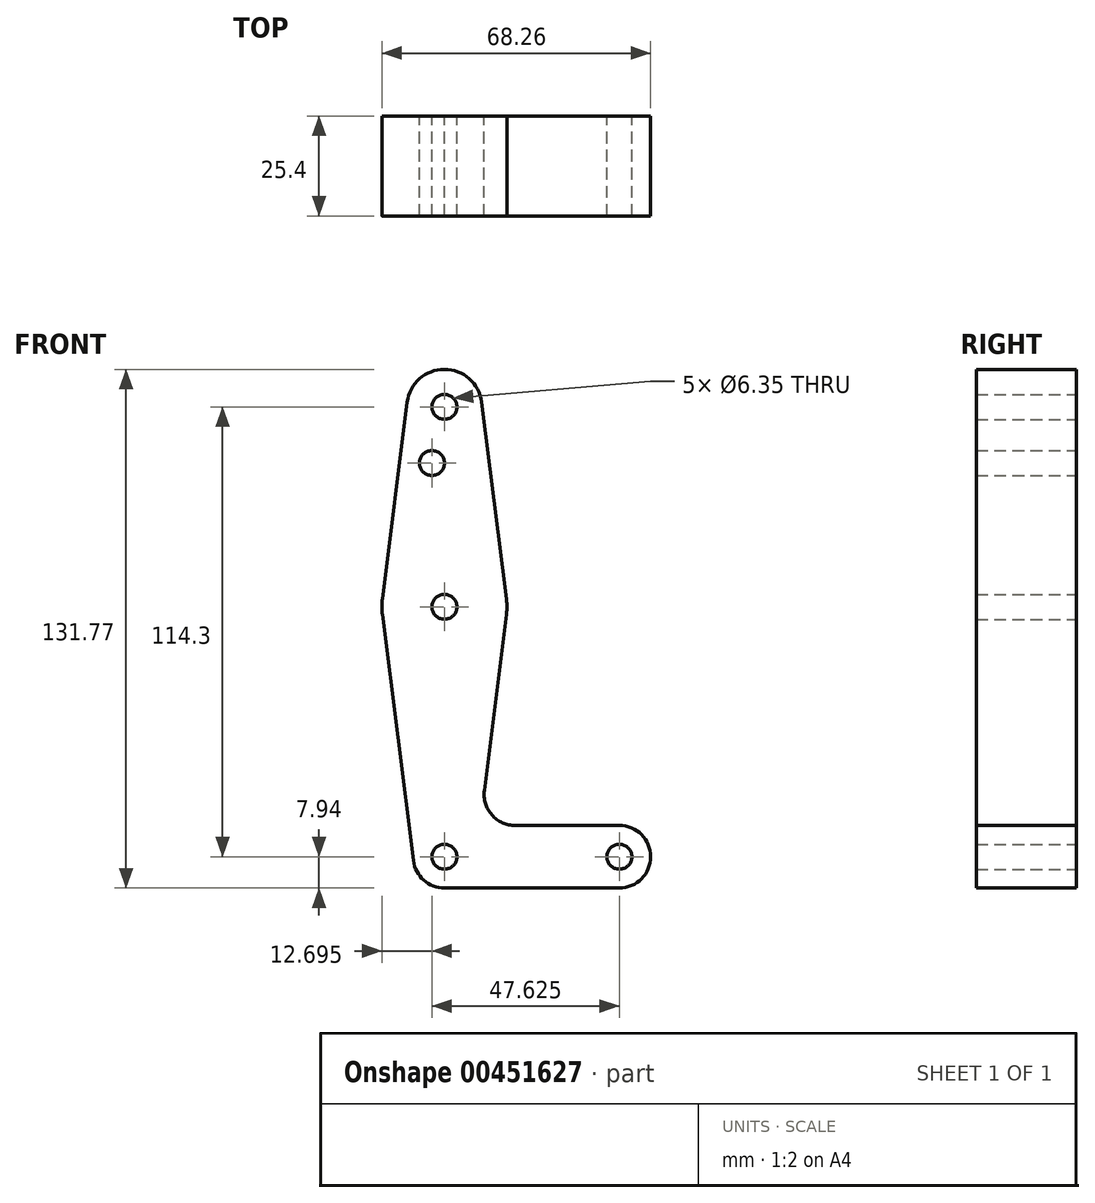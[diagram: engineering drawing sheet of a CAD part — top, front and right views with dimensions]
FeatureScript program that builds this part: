
annotation { "Feature Type Name" : "Feature", "Feature Type Description" : "" }
export const myFeature = defineFeature(function(context is Context, id is Id, definition is map)
    precondition{}
    {
        {
            var Q0;
            Q0=qCreatedBy(makeId("Front.planeOp"),FACE);
            var sketch = newSketch(context, id + "F0", { "sketchPlane" : qUnion([Q0])});
            skLineSegment(sketch, "E0", {"start": v(0, 0) * mm, "end": v(0, 114.3) * mm, "construction": true});
            skLineSegment(sketch, "E1", {"start": v(0, 0) * mm, "end": v(44.45, 0) * mm, "construction": true});
            skCircle(sketch, "E2", {"center": v(0, 114.3) * mm, "radius": 9.53 * mm});
            skCircle(sketch, "E3", {"center": v(0, 63.5) * mm, "radius": 15.88 * mm});
            skCircle(sketch, "E4", {"center": v(0, 0) * mm, "radius": 7.94 * mm});
            skCircle(sketch, "E5", {"center": v(44.45, 0) * mm, "radius": 7.94 * mm});
            skLineSegment(sketch, "E6", {"start": v(15.75, 61.52) * mm, "end": v(10.13, 16.88) * mm});
            skLineSegment(sketch, "E7", {"start": v(-15.75, 65.48) * mm, "end": v(-9.45, 115.5) * mm});
            skLineSegment(sketch, "E8", {"start": v(9.45, 115.5) * mm, "end": v(15.75, 65.48) * mm});
            skLineSegment(sketch, "E9", {"start": v(0, -7.94) * mm, "end": v(44.45, -7.94) * mm});
            skLineSegment(sketch, "E10", {"start": v(18.01, 7.94) * mm, "end": v(44.45, 7.94) * mm});
            skCircle(sketch, "E11", {"center": v(-3.18, 100.03) * mm, "radius": 3.18 * mm});
            skCircle(sketch, "E12", {"center": v(0, 63.5) * mm, "radius": 3.18 * mm});
            skCircle(sketch, "E13", {"center": v(0, 0) * mm, "radius": 3.18 * mm});
            skCircle(sketch, "E14", {"center": v(44.45, 0) * mm, "radius": 3.18 * mm});
            skCircle(sketch, "E15", {"center": v(0, 114.3) * mm, "radius": 3.18 * mm});
            skArc(sketch, "E16.filletArc", {"start": v(10.13, 16.88) * mm, "mid": v(12.05, 10.63) * mm, "end": v(18.01, 7.94) * mm});
            skLineSegment(sketch, "E17", {"start": v(-15.75, 61.52) * mm, "end": v(-7.88, -1) * mm});
            skSolve(sketch);
        }
        {
            var Q0;
            Q0=makeQuery(id+"F0.imprint","IMPRINT",FACE,{"disambiguationData":[TD([[makeQuery(id+"F0.imprint","IMPRINT",EDGE,{"derivedFrom":sQuery(id+"F0.wireOp",EDGE,"E15")}),-1.0]])]});
            var Q1;
            {var subQ1=sQuery(id+"F0.wireOp",EDGE,"E7");Q1=makeQuery(id+"F0.imprint","IMPRINT",FACE,{"disambiguationData":[TD([[makeQuery(id+"F0.imprint","IMPRINT",EDGE,{"derivedFrom":subQ1}),-1.0]])]});}
            var Q2;
            Q2=makeQuery(id+"F0.imprint","IMPRINT",FACE,{"disambiguationData":[TD([[makeQuery(id+"F0.imprint","IMPRINT",EDGE,{"derivedFrom":sQuery(id+"F0.wireOp",EDGE,"E12")}),-1.0]])]});
            var Q3;
            {var subQ0=sQuery(id+"F0.wireOp",EDGE,"E6");Q3=makeQuery(id+"F0.imprint","IMPRINT",FACE,{"disambiguationData":[TD([[makeQuery(id+"F0.imprint","IMPRINT",EDGE,{"derivedFrom":subQ0}),-1.0]])]});}
            var Q4;
            Q4=makeQuery(id+"F0.imprint","IMPRINT",FACE,{"disambiguationData":[TD([[makeQuery(id+"F0.imprint","IMPRINT",EDGE,{"derivedFrom":sQuery(id+"F0.wireOp",EDGE,"E13")}),-1.0]])]});
            var Q5;
            Q5=makeQuery(id+"F0.imprint","IMPRINT",FACE,{"disambiguationData":[TD([[makeQuery(id+"F0.imprint","IMPRINT",EDGE,{"derivedFrom":sQuery(id+"F0.wireOp",EDGE,"E14")}),-1.0]])]});
            var Q6;
            Q6=sQuery(id+"F0.wireOp",EDGE,"E12");
            var Q7;
            Q7=sQuery(id+"F0.wireOp",EDGE,"E11");
            var Q8;
            Q8=sQuery(id+"F0.wireOp",EDGE,"E10");
            var Q9;
            Q9=sQuery(id+"F0.wireOp",EDGE,"E9");
            var Q10;
            Q10=sQuery(id+"F0.wireOp",EDGE,"E8");
            var Q11;
            Q11=sQuery(id+"F0.wireOp",EDGE,"E7");
            var Q12;
            Q12=sQuery(id+"F0.wireOp",EDGE,"E6");
            var Q13;
            Q13=sQuery(id+"F0.wireOp",EDGE,"E5");
            var Q14;
            Q14=sQuery(id+"F0.wireOp",EDGE,"E3");
            var Q15;
            Q15=sQuery(id+"F0.wireOp",EDGE,"E2");
            var Q16;
            Q16=sQuery(id+"F0.wireOp",EDGE,"E15");
            var Q17;
            Q17=sQuery(id+"F0.wireOp",EDGE,"E14");
            var Q18;
            Q18=sQuery(id+"F0.wireOp",EDGE,"E17");
            var Q19;
            Q19=sQuery(id+"F0.wireOp",EDGE,"E16.filletArc");
            var Q20;
            Q20=sQuery(id+"F0.wireOp",EDGE,"E4");
            var Q21;
            Q21=sQuery(id+"F0.wireOp",EDGE,"E13");
            extrude(context, id + "F1", {"entities" : qUnion([Q0, Q1, Q2, Q3, Q4, Q5]), "surfaceEntities" : qUnion([Q6, Q7, Q8, Q9, Q10, Q11, Q12, Q13, Q14, Q15, Q16, Q17, Q18, Q19, Q20, Q21]), "depth" : 25.4 * mm});
        }
    });
